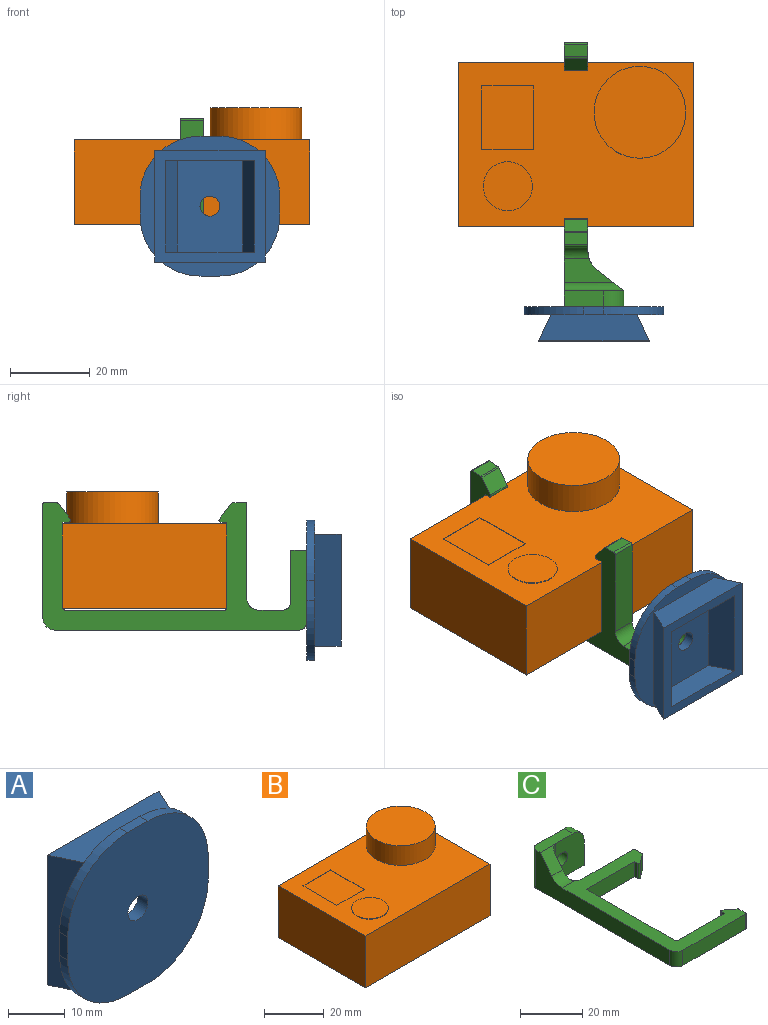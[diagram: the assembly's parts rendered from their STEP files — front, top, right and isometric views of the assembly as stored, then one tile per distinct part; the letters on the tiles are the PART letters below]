
ASSEMBLY  parts=3 mates=2
PART A: 21 faces, bbox 35x8.6x35 mm
  f0: plane 28x27.7mm, normal (0,1,0), area 265.6mm2, adj f7,f8,f9,f10,f11,f12,f13,f14
  f1: plane 35x35mm, normal (0,1,0), area 429.9mm2, adj f2,f3,f4,f5,f7,f8,f9,f10
  f2: plane 5x2mm, normal (-1,0,0), area 10mm2, adj f1,f6,f17,f20
  f3: plane 5x2mm, normal (0,0,1), area 10mm2, adj f1,f6,f17,f18
  f4: plane 5x2mm, normal (1,0,0), area 10mm2, adj f1,f6,f18,f19
  f5: plane 5x2mm, normal (0,0,-1), area 10mm2, adj f1,f6,f19,f20
  f6: plane 35x35mm, normal (0,-1,0), area 1012.2mm2, adj f2,f3,f4,f5,f16,f17,f18,f19
  f7: plane 28x6.6mm, normal (-0.91,-0.43,0), area 204.2mm2, adj f0,f1,f8,f10
  f8: plane 27.7x6.6mm, normal (0,0,-1), area 162.4mm2, adj f0,f1,f7,f9
  f9: plane 28x6.6mm, normal (0.91,-0.43,0), area 204.2mm2, adj f0,f1,f8,f10
  f10: plane 27.7x6.6mm, normal (0,0,1), area 162.4mm2, adj f0,f1,f7,f9
  f11: plane 22.18x6.1mm, normal (0,0,-1), area 117.8mm2, adj f0,f12,f14,f15
  f12: plane 23x6.1mm, normal (-0.91,0.43,0), area 155mm2, adj f0,f11,f13,f15
  f13: plane 22.18x6.1mm, normal (0,0,1), area 117.8mm2, adj f0,f12,f14,f15
  f14: plane 23x6.1mm, normal (0.91,0.43,0), area 155mm2, adj f0,f11,f13,f15
  f15: plane 23x16.45mm, normal (0,1,0), area 358.6mm2, adj f11,f12,f13,f14,f16
  f16: cylinder r=2.5mm len=5mm, axis (0,1,0), area 39.3mm2, adj f6,f15
  f17: cylinder r=15mm len=15mm, axis (0,-1,0), area 47.1mm2, adj f1,f2,f3,f6
  f18: cylinder r=15mm len=15mm, axis (0,1,0), area 47.1mm2, adj f1,f3,f4,f6
  f19: cylinder r=15mm len=15mm, axis (0,-1,0), area 47.1mm2, adj f1,f4,f5,f6
  f20: cylinder r=15mm len=15mm, axis (0,1,0), area 47.1mm2, adj f1,f2,f5,f6
PART B: 17 faces, bbox 59x41.3x29.2 mm
  f0: plane 41.2x21.2mm, normal (1,0,0), area 873.4mm2, adj f1,f3,f4,f5
  f1: plane 59x21.2mm, normal (0,1,0), area 1122.1mm2, adj f0,f2,f4,f5,f8
  f2: plane 41.2x21.2mm, normal (-1,0,0), area 873.4mm2, adj f1,f3,f4,f5
  f3: plane 59x21.2mm, normal (0,-1,0), area 1250.8mm2, adj f0,f2,f4,f5
  f4: plane 59x41.2mm, normal (0,0,1), area 1688.5mm2, adj f0,f1,f2,f3,f6,f10,f11,f12
  f5: plane 59x41.2mm, normal (0,0,-1), area 2430.8mm2, adj f0,f1,f2,f3
  f6: cylinder r=11.5mm len=23mm, axis (0,0,-1), area 578.1mm2, adj f4,f7
  f7: plane 23x23mm, normal (0,0,1), area 415.5mm2, adj f6
  f8: cylinder r=6.4mm len=12.8mm, axis (0,-1,0), area 4mm2, adj f1,f9
  f9: plane 12.8x12.8mm, normal (0,1,0), area 128.7mm2, adj f8
  f10: plane 16x0.1mm, normal (1,0,0), area 1.6mm2, adj f4,f11,f13,f14
  f11: plane 13x0.1mm, normal (0,1,0), area 1.3mm2, adj f4,f10,f12,f14
  f12: plane 16x0.1mm, normal (-1,0,0), area 1.6mm2, adj f4,f11,f13,f14
  f13: plane 13x0.1mm, normal (0,-1,0), area 1.3mm2, adj f4,f10,f12,f14
  f14: plane 16x13mm, normal (0,0,1), area 208mm2, adj f10,f11,f12,f13
  f15: cylinder r=6.15mm len=12.3mm, axis (0,0,-1), area 7.7mm2, adj f4,f16
  f16: plane 12.3x12.3mm, normal (0,0,1), area 118.8mm2, adj f15
PART C: 35 faces, bbox 32.1x66.1x15 mm
  f0: plane 61.1x15mm, normal (-1,0,0), area 417.3mm2, adj f13,f14,f18,f19,f23,f32,f34
  f1: plane 12.43x6mm, normal (1,0,0), area 53.1mm2, adj f14,f19,f22,f33,f34
  f2: plane 23.58x6mm, normal (0,1,0), area 141.5mm2, adj f13,f14,f22,f31
  f3: plane 28.58x6mm, normal (0,-1,0), area 171.5mm2, adj f13,f14,f23,f24
  f4: plane 6x2.99mm, normal (1,0.06,0), area 18mm2, adj f13,f14,f24,f25
  f5: plane 6x3.91mm, normal (0.61,0.79,0), area 29.5mm2, adj f13,f14,f25,f26
  f6: plane 6x1.49mm, normal (-1,0,0), area 8.9mm2, adj f7,f13,f14,f26
  f7: plane 21.5x6mm, normal (0,1,0), area 129mm2, adj f6,f13,f14,f27
  f8: plane 40.1x6mm, normal (1,0,0), area 240.6mm2, adj f13,f14,f27,f28
  f9: plane 21.5x6mm, normal (0,-1,0), area 129mm2, adj f10,f13,f14,f28
  f10: plane 6x1.49mm, normal (-1,0,0), area 8.9mm2, adj f9,f13,f14,f29
  f11: plane 6x3.91mm, normal (0.61,-0.79,0), area 29.5mm2, adj f13,f14,f29,f30
  f12: plane 6x2.99mm, normal (1,-0.06,0), area 18mm2, adj f13,f14,f30,f31
  f13: plane 52.17x32.08mm, normal (0,0,1), area 535.8mm2, adj f0,f2,f3,f4,f5,f6,f7,f8
  f14: plane 66.1x32.08mm, normal (0,0,-1), area 665.9mm2, adj f0,f1,f2,f3,f4,f5,f6,f7
  f15: plane 18x15mm, normal (0,1,0), area 245mm2, adj f14,f16,f18,f20,f21,f32
  f16: plane 10x4mm, normal (1,0,0), area 40mm2, adj f14,f15,f17,f20
  f17: plane 15x13mm, normal (0,-1,0), area 170mm2, adj f14,f16,f18,f20,f21,f33
  f18: plane 15x4mm, normal (0,0,1), area 59.1mm2, adj f0,f15,f17,f19,f20,f32
  f19: plane 7x6.68mm, normal (0,-0.79,0.61), area 43.7mm2, adj f0,f1,f18,f33,f34
  f20: cylinder r=5mm len=5mm, axis (0,1,0), area 31.4mm2, adj f15,f16,f17,f18
  f21: cylinder r=2.5mm len=5mm, axis (0,1,0), area 62.8mm2, adj f15,f17
  f22: cylinder r=3mm len=6.32mm, axis (0,0,1), area 28.5mm2, adj f1,f2,f13,f14,f34
  f23: cylinder r=3mm len=6mm, axis (0,0,-1), area 28.3mm2, adj f0,f3,f13,f14
  f24: cylinder r=0.5mm len=6mm, axis (0,0,1), area 4.9mm2, adj f3,f4,f13,f14
  f25: cylinder r=0.5mm len=6mm, axis (0,0,1), area 2.6mm2, adj f4,f5,f13,f14
  f26: cylinder r=0.5mm len=6mm, axis (0,0,-1), area 6.7mm2, adj f5,f6,f13,f14
  f27: cylinder r=0.5mm len=6mm, axis (0,0,1), area 4.7mm2, adj f7,f8,f13,f14
  f28: cylinder r=0.5mm len=6mm, axis (0,0,-1), area 4.7mm2, adj f8,f9,f13,f14
  f29: cylinder r=0.5mm len=6mm, axis (0,0,-1), area 6.7mm2, adj f10,f11,f13,f14
  f30: cylinder r=0.5mm len=6mm, axis (0,0,1), area 2.6mm2, adj f11,f12,f13,f14
  f31: cylinder r=0.5mm len=6mm, axis (0,0,1), area 4.9mm2, adj f2,f12,f13,f14
  f32: cylinder r=2mm len=15mm, axis (0,0,-1), area 47.1mm2, adj f0,f14,f15,f18
  f33: cylinder r=2mm len=15mm, axis (0,0,1), area 44.2mm2, adj f1,f14,f17,f19
  f34: cylinder r=6mm len=5.71mm, axis (1,0,0), area 27.7mm2, adj f0,f1,f13,f19,f22
PLACE A rot(axis=(-1,0,0),180deg) t=(-4.34,51.76,9.34)mm
PLACE B t=(-14.84,3.81,-2.76)mm
PLACE C rot(axis=(-0.71,0,-0.71),180deg) t=(-17.84,3.76,7.84)mm
MATE revolute C.f21 <-> A.f16  axis (0,-1,0) through (-10.34,-36.79,1.84)mm
MATE planar B.f3 <-> C.f9  axis (0,-1,0) through (-14.84,-16.79,7.84)mm
